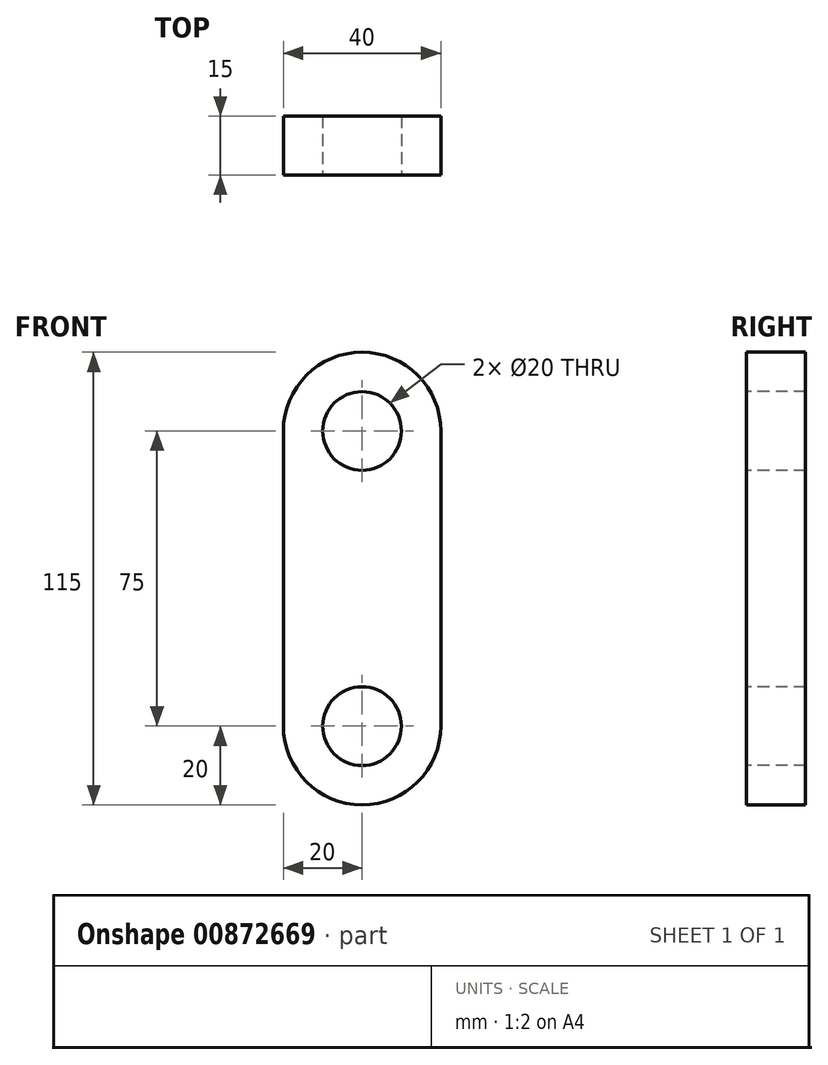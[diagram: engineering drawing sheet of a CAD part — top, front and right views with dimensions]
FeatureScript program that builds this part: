
annotation { "Feature Type Name" : "Feature", "Feature Type Description" : "" }
export const myFeature = defineFeature(function(context is Context, id is Id, definition is map)
    precondition{}
    {
        {
            var Q0;
            Q0=qCreatedBy(makeId("Front.planeOp"),FACE);
            var sketch = newSketch(context, id + "F0", { "sketchPlane" : qUnion([Q0])});
            skCircle(sketch, "E0", {"center": v(0, 0) * mm, "radius": 20 * mm});
            skCircle(sketch, "E1", {"center": v(0, 75) * mm, "radius": 20 * mm});
            skLineSegment(sketch, "E2", {"start": v(-20, 75) * mm, "end": v(-20, 0) * mm});
            skLineSegment(sketch, "E3", {"start": v(20, 75) * mm, "end": v(20, 0) * mm});
            skSolve(sketch);
        }
        {
            var Q0;
            {var subQ0=sQuery(id+"F0.wireOp",EDGE,"E1");var subQ1=makeQuery(id+"F0.imprint","INTERSECT",VERTEX,{"derivedFrom":[subQ0,sQuery(id+"F0.wireOp",EDGE,"E2")]});Q0=makeQuery(id+"F0.imprint","IMPRINT",FACE,{"disambiguationData":[TD([[makeQuery(id+"F0.imprint","IMPRINT",EDGE,{"disambiguationData":[TD([[subQ1,1.0]])],"derivedFrom":subQ0}),1.0]])]});}
            var Q1;
            {var subQ0=sQuery(id+"F0.wireOp",EDGE,"E2");Q1=makeQuery(id+"F0.imprint","IMPRINT",FACE,{"disambiguationData":[TD([[makeQuery(id+"F0.imprint","IMPRINT",EDGE,{"derivedFrom":subQ0}),1.0]])]});}
            var Q2;
            {var subQ0=sQuery(id+"F0.wireOp",EDGE,"E0");var subQ1=makeQuery(id+"F0.imprint","INTERSECT",VERTEX,{"derivedFrom":[subQ0,sQuery(id+"F0.wireOp",EDGE,"E2")]});Q2=makeQuery(id+"F0.imprint","IMPRINT",FACE,{"disambiguationData":[TD([[makeQuery(id+"F0.imprint","IMPRINT",EDGE,{"disambiguationData":[TD([[subQ1,1.0]])],"derivedFrom":subQ0}),1.0]])]});}
            extrude(context, id + "F1", {"entities" : qUnion([Q0, Q1, Q2]), "depth" : 15 * mm, "offsetDistance" : 25 * mm});
        }
        {
            var Q0;
            Q0=makeQuery(id+"F1.opExtrude","CAP_FACE",FACE,{"disambiguationData":[OSD([sQuery(id+"F0.wireOp",EDGE,"E0"),sQuery(id+"F0.wireOp",EDGE,"E1"),sQuery(id+"F0.wireOp",EDGE,"E2"),sQuery(id+"F0.wireOp",EDGE,"E3")])],"isStart":false});
            var sketch = newSketch(context, id + "F2", { "sketchPlane" : qUnion([Q0])});
            skCircle(sketch, "E4", {"center": v(0, 75) * mm, "radius": 10 * mm});
            skCircle(sketch, "E5", {"center": v(0, 0) * mm, "radius": 10 * mm});
            skSolve(sketch);
        }
        {
            var Q0;
            Q0=makeQuery(id+"F2.imprint","IMPRINT",FACE,{"disambiguationData":[TD([[makeQuery(id+"F2.imprint","IMPRINT",EDGE,{"derivedFrom":sQuery(id+"F2.wireOp",EDGE,"E4")}),1.0]])]});
            var Q1;
            Q1=makeQuery(id+"F2.imprint","IMPRINT",FACE,{"disambiguationData":[TD([[makeQuery(id+"F2.imprint","IMPRINT",EDGE,{"derivedFrom":sQuery(id+"F2.wireOp",EDGE,"E5")}),1.0]])]});
            extrude(context, id + "F3", {"entities" : qUnion([Q0, Q1]), "operationType" : NewBodyOperationType.REMOVE, "oppositeDirection" : true, "depth" : 25 * mm, "offsetDistance" : 25 * mm});
        }
    });
